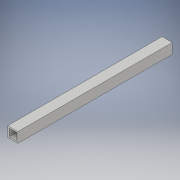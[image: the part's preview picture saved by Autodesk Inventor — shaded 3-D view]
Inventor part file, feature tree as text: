
AUTODESK INVENTOR PART (.ipt)
format: ipt  version: 2018 (Build 220112000, 112)  size: 97,280 bytes
history: native  units: in
note: dims shown in document units (in); Inventor stores cm internally (conversion verified against a paired STEP export)
features: extrude x1, sketch x1
ambient origin geometry x8: Origin, YZ Plane, XZ Plane, XY Plane, X Axis, Y Axis, Z Axis, Center Point
bodies: Solid1 (feature_tree)
feature tree (2):
  extrude  "Extrusion1"  Depth=1.0in
  sketch  "Sketch1"  dims[d0=1.0in d1=1.0in d2=0.125in d3=15.11in d4=0.0in]
